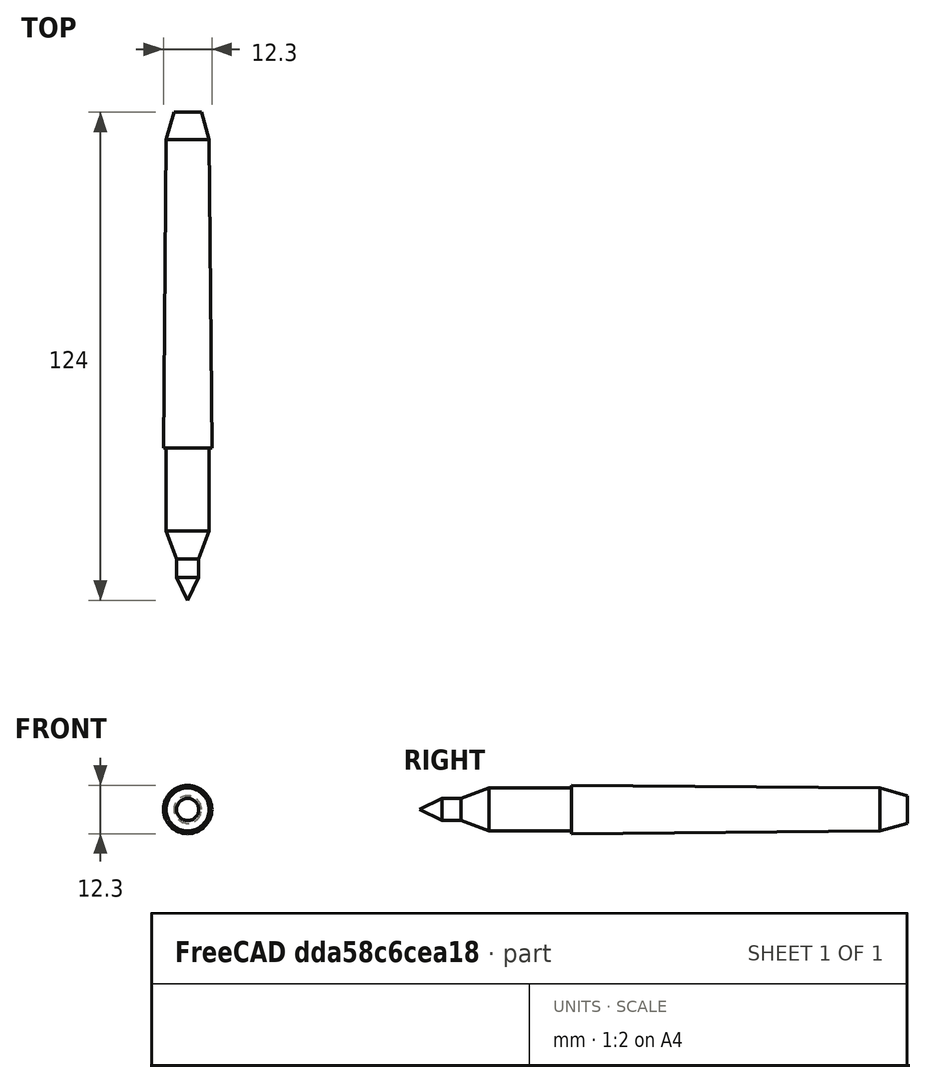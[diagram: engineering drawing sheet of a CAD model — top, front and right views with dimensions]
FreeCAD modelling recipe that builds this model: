
FCSTD DOCUMENT  (FreeCAD 0.18R)
Label: sharpie
License: All rights reserved
LicenseURL: http://en.wikipedia.org/wiki/All_rights_reserved
objects: Sketcher::SketchObject×1, PartDesign::Revolution×1, PartDesign::Body×1
note: 4 computed .brp shape members not serialized (recipe doc carries the construction recipe); baked Part::Feature solids carry a one-line shape summary decoded from their .brp

FEATURE [Sketcher::SketchObject] Sketch
  MapMode = 5
  Support = -> [XY_Plane]
  sketch-geometry (11):
    g0: LineSegment StartX=-3.5 StartY=124 StartZ=0 EndX=0 EndY=124 EndZ=0
    g1: LineSegment StartX=-3.5 StartY=124 StartZ=0 EndX=-5.45 EndY=117 EndZ=0
    g2: GeomPoint X=-6.15 Y=38.65 Z=0
    g3: LineSegment StartX=-5.45 StartY=117 StartZ=0 EndX=-6.15 EndY=38.65 EndZ=0
    g4: LineSegment StartX=-6.15 StartY=38.65 StartZ=0 EndX=-5.45 EndY=38.65 EndZ=0
    g5: LineSegment StartX=-5.45 StartY=38.65 StartZ=0 EndX=-5.45 EndY=17.65 EndZ=0
    g6: GeomPoint X=-2.815 Y=10.5 Z=0
    g7: LineSegment StartX=-2.815 StartY=10.5 StartZ=0 EndX=-2.815 EndY=5.75 EndZ=0
    g8: LineSegment StartX=-2.815 StartY=5.75 StartZ=0 EndX=0 EndY=0 EndZ=0
    g9: LineSegment StartX=-5.45 StartY=17.65 StartZ=0 EndX=-2.815 EndY=10.5 EndZ=0
    g10: LineSegment StartX=0 StartY=0 StartZ=0 EndX=0 EndY=124 EndZ=0
  constraints (28):
    c: Horizontal(g0)
    c: DistanceY(g-1,g0) = 124
    c: PointOnObject(g0,g-2)
    c: DistanceX(g0,g0) = 3.5
    c: DistanceY(g1,g0) = 7
    c: DistanceX(g1,g-1) = 5.45
    c: DistanceY(g2,g0) = 85.35
    c: DistanceX(g2,g-1) = 6.15
    c: Coincident(g3,g1)
    c: Coincident(g3,g2)
    c: Coincident(g4,g2)
    c: Horizontal(g4)
    c: DistanceX(g4,g-1) = 5.45
    c: Coincident(g5,g4)
    c: Vertical(g5)
    c: DistanceY(g5,g5) = 21
    c: DistanceX(g6,g-1) = 2.815
    c: DistanceY(g-1,g6) = 10.5
    c: Coincident(g7,g6)
    c: Vertical(g7)
    c: Coincident(g8,g7)
    c: Coincident(g8,g-1)
    c: DistanceY(g7,g7) = 4.75
    c: Coincident(g9,g5)
    c: Coincident(g9,g6)
    c: Coincident(g10,g8)
    c: Coincident(g10,g0)
    c: Coincident(g0,g1)
FEATURE [PartDesign::Revolution] Revolution
  Angle = 360
  Axis = (0,1,0)
  Base = (0,0,0)
  Profile = -> Sketch
  ReferenceAxis = -> Sketch [V_Axis]
FEATURE [PartDesign::Body] Body
  Group = -> [Sketch,Revolution]
  Origin = -> Origin
  Tip = -> Revolution
